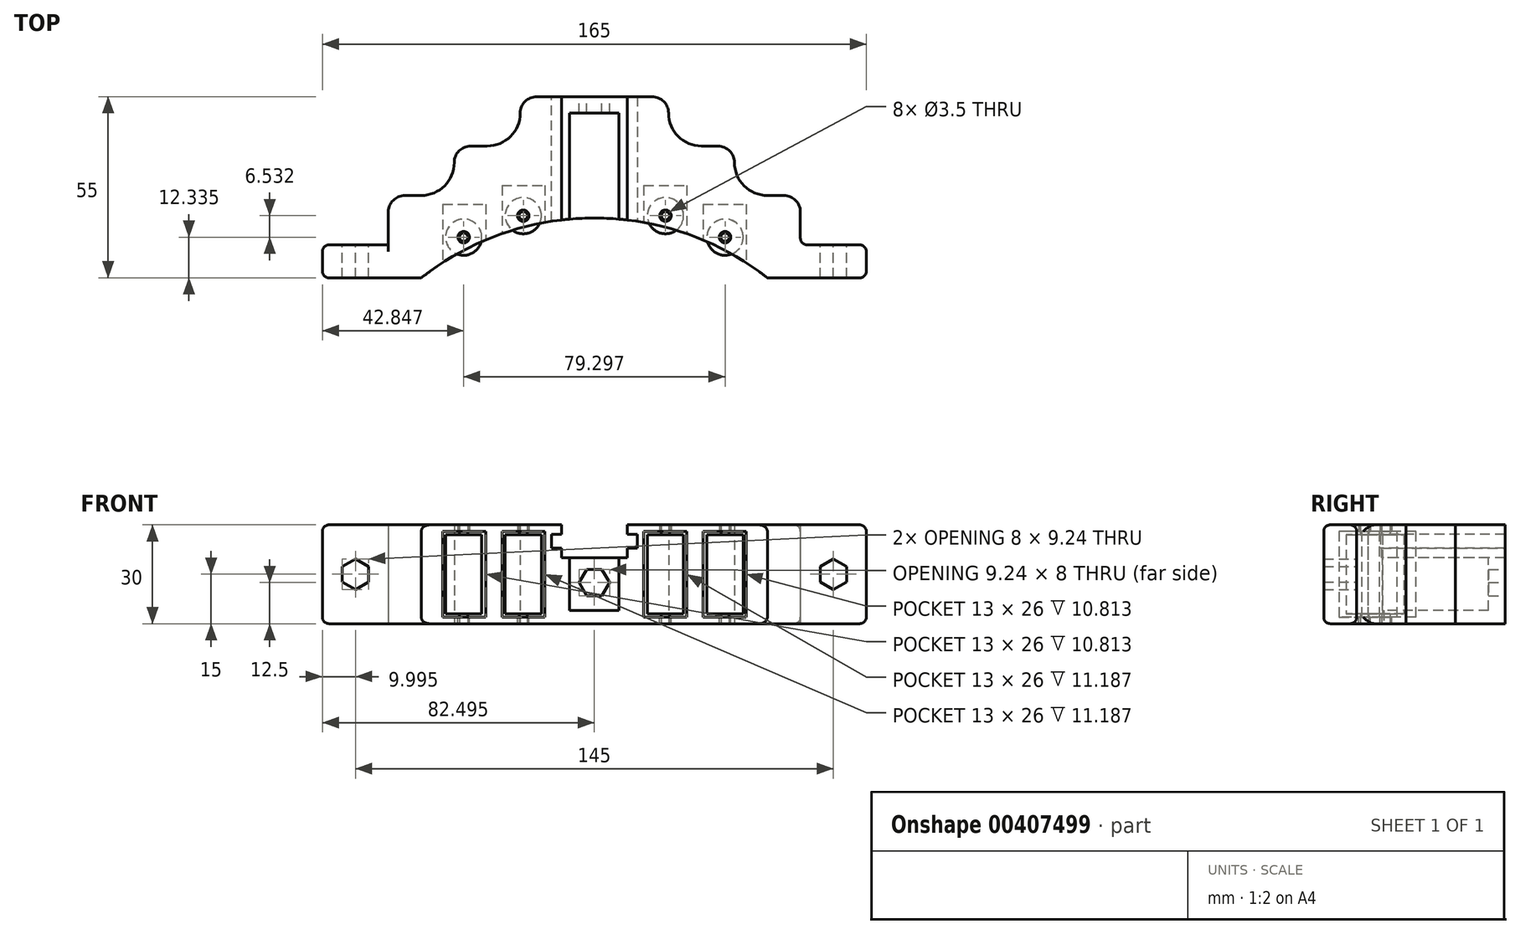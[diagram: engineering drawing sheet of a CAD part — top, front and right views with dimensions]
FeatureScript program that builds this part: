
annotation { "Feature Type Name" : "Feature", "Feature Type Description" : "" }
export const myFeature = defineFeature(function(context is Context, id is Id, definition is map)
    precondition{}
    {
        {
            var Q0;
            Q0=qCreatedBy(makeId("Top.planeOp"),FACE);
            var sketch = newSketch(context, id + "F0", { "sketchPlane" : qUnion([Q0])});
            skLineSegment(sketch, "E0", {"start": v(-87.77, -10.35) * mm, "end": v(-57.77, -10.35) * mm});
            skLineSegment(sketch, "E1", {"start": v(47.23, -10.35) * mm, "end": v(77.23, -10.35) * mm});
            skArc(sketch, "E2", {"start": v(47.23, -10.35) * mm, "mid": v(-5.27, 7.8) * mm, "end": v(-57.77, -10.35) * mm});
            skLineSegment(sketch, "E3", {"start": v(-87.77, -10.35) * mm, "end": v(-87.77, -0.35) * mm});
            skLineSegment(sketch, "E4", {"start": v(-87.77, -0.35) * mm, "end": v(-67.77, -0.35) * mm});
            skLineSegment(sketch, "E5", {"start": v(-67.77, -0.35) * mm, "end": v(-67.77, 14.65) * mm});
            skLineSegment(sketch, "E6", {"start": v(-67.77, 14.65) * mm, "end": v(-47.77, 14.65) * mm});
            skLineSegment(sketch, "E7", {"start": v(-47.77, 14.65) * mm, "end": v(-47.77, 29.65) * mm});
            skLineSegment(sketch, "E8", {"start": v(-47.77, 29.65) * mm, "end": v(-27.77, 29.65) * mm});
            skLineSegment(sketch, "E9", {"start": v(-27.77, 29.65) * mm, "end": v(-27.77, 44.65) * mm});
            skLineSegment(sketch, "E10", {"start": v(-5.27, -77.2) * mm, "end": v(-5.27, 79.15) * mm, "construction": true});
            skPoint(sketch, "E10.endSnap0", {"position": v(-5.27, 7.8) * mm});
            skLineSegment(sketch, "E11", {"start": v(77.23, -10.35) * mm, "end": v(77.23, -0.35) * mm});
            skLineSegment(sketch, "E12", {"start": v(77.23, -0.35) * mm, "end": v(57.23, -0.35) * mm});
            skLineSegment(sketch, "E13", {"start": v(57.23, -0.35) * mm, "end": v(57.23, 14.65) * mm});
            skLineSegment(sketch, "E14", {"start": v(57.23, 14.65) * mm, "end": v(37.23, 14.65) * mm});
            skLineSegment(sketch, "E15", {"start": v(37.23, 14.65) * mm, "end": v(37.23, 29.65) * mm});
            skLineSegment(sketch, "E16", {"start": v(37.23, 29.65) * mm, "end": v(17.23, 29.65) * mm});
            skLineSegment(sketch, "E17", {"start": v(17.23, 29.65) * mm, "end": v(17.23, 44.65) * mm});
            skLineSegment(sketch, "E18", {"start": v(-27.77, 44.65) * mm, "end": v(17.23, 44.65) * mm});
            skSolve(sketch);
        }
        {
            var Q0;
            Q0=makeQuery(id+"F0.imprint","IMPRINT",FACE,{"disambiguationData":[TD([[makeQuery(id+"F0.imprint","IMPRINT",EDGE,{"derivedFrom":sQuery(id+"F0.wireOp",EDGE,"E0")}),1.0]])]});
            extrude(context, id + "F1", {"entities" : qUnion([Q0]), "depth" : 30 * mm});
        }
        {
            var Q0;
            Q0=makeQuery(id+"F1.opExtrude","SWEPT_EDGE",EDGE,{"disambiguationData":[OSD([sQuery(id+"F0.wireOp",EDGE,"E6"),sQuery(id+"F0.wireOp",EDGE,"E7")])]});
            var Q1;
            Q1=makeQuery(id+"F1.opExtrude","SWEPT_EDGE",EDGE,{"disambiguationData":[OSD([sQuery(id+"F0.wireOp",EDGE,"E8"),sQuery(id+"F0.wireOp",EDGE,"E9")])]});
            var Q2;
            Q2=makeQuery(id+"F1.opExtrude","SWEPT_EDGE",EDGE,{"disambiguationData":[OSD([sQuery(id+"F0.wireOp",EDGE,"E16"),sQuery(id+"F0.wireOp",EDGE,"E17")])]});
            var Q3;
            Q3=makeQuery(id+"F1.opExtrude","SWEPT_EDGE",EDGE,{"disambiguationData":[OSD([sQuery(id+"F0.wireOp",EDGE,"E14"),sQuery(id+"F0.wireOp",EDGE,"E15")])]});
            fillet(context, id + "F2", {"entities" : qUnion([Q0, Q1, Q2, Q3]), "radius" : 10 * mm, "tangentPropagation" : true, "allowEdgeOverflow" : false});
        }
        {
            var Q0;
            Q0=makeQuery(id+"F1.opExtrude","SWEPT_EDGE",EDGE,{"disambiguationData":[OSD([sQuery(id+"F0.wireOp",EDGE,"E5"),sQuery(id+"F0.wireOp",EDGE,"E6")])]});
            var Q1;
            Q1=makeQuery(id+"F1.opExtrude","SWEPT_EDGE",EDGE,{"disambiguationData":[OSD([sQuery(id+"F0.wireOp",EDGE,"E7"),sQuery(id+"F0.wireOp",EDGE,"E8")])]});
            var Q2;
            Q2=makeQuery(id+"F1.opExtrude","SWEPT_EDGE",EDGE,{"disambiguationData":[OSD([sQuery(id+"F0.wireOp",EDGE,"E9"),sQuery(id+"F0.wireOp",EDGE,"E18")])]});
            var Q3;
            Q3=makeQuery(id+"F1.opExtrude","SWEPT_EDGE",EDGE,{"disambiguationData":[OSD([sQuery(id+"F0.wireOp",EDGE,"E17"),sQuery(id+"F0.wireOp",EDGE,"E18")])]});
            var Q4;
            Q4=makeQuery(id+"F1.opExtrude","SWEPT_EDGE",EDGE,{"disambiguationData":[OSD([sQuery(id+"F0.wireOp",EDGE,"E15"),sQuery(id+"F0.wireOp",EDGE,"E16")])]});
            var Q5;
            Q5=makeQuery(id+"F1.opExtrude","SWEPT_EDGE",EDGE,{"disambiguationData":[OSD([sQuery(id+"F0.wireOp",EDGE,"E13"),sQuery(id+"F0.wireOp",EDGE,"E14")])]});
            fillet(context, id + "F3", {"entities" : qUnion([Q0, Q1, Q2, Q3, Q4, Q5]), "radius" : 5 * mm, "tangentPropagation" : true, "allowEdgeOverflow" : false});
        }
        {
            var Q0;
            Q0=makeQuery(id+"F1.opExtrude","SWEPT_FACE",FACE,{"disambiguationData":[OSD([sQuery(id+"F0.wireOp",EDGE,"E0")])]});
            cPlane(context, id + "F4", {"entities" : qUnion([Q0]), "cplaneType" : CPlaneType.OFFSET, "offset" : 0 * mm, "width" : 150 * mm, "height" : 150 * mm});
        }
        {
            var Q0;
            Q0=qCreatedBy(id+"F4.planeOp",FACE);
            var sketch = newSketch(context, id + "F5", { "sketchPlane" : qUnion([Q0])});
            skLineSegment(sketch, "E19", {"start": v(-51.27, 28) * mm, "end": v(-38.27, 28) * mm});
            skLineSegment(sketch, "E20", {"start": v(-38.27, 28) * mm, "end": v(-38.27, 2) * mm});
            skLineSegment(sketch, "E21", {"start": v(-38.27, 2) * mm, "end": v(-51.27, 2) * mm});
            skLineSegment(sketch, "E22", {"start": v(-51.27, 2) * mm, "end": v(-51.27, 28) * mm});
            skLineSegment(sketch, "E23", {"start": v(-33.27, 28) * mm, "end": v(-20.27, 28) * mm});
            skLineSegment(sketch, "E24", {"start": v(-20.27, 28) * mm, "end": v(-20.27, 2) * mm});
            skLineSegment(sketch, "E25", {"start": v(-20.27, 2) * mm, "end": v(-33.27, 2) * mm});
            skLineSegment(sketch, "E26", {"start": v(-33.27, 2) * mm, "end": v(-33.27, 28) * mm});
            skLineSegment(sketch, "E27", {"start": v(9.73, 28) * mm, "end": v(22.73, 28) * mm});
            skLineSegment(sketch, "E28", {"start": v(22.73, 28) * mm, "end": v(22.73, 2) * mm});
            skLineSegment(sketch, "E29", {"start": v(22.73, 2) * mm, "end": v(9.73, 2) * mm});
            skLineSegment(sketch, "E30", {"start": v(9.73, 2) * mm, "end": v(9.73, 28) * mm});
            skLineSegment(sketch, "E31", {"start": v(27.73, 28) * mm, "end": v(40.73, 28) * mm});
            skLineSegment(sketch, "E32", {"start": v(40.73, 28) * mm, "end": v(40.73, 2) * mm});
            skLineSegment(sketch, "E33", {"start": v(40.73, 2) * mm, "end": v(27.73, 2) * mm});
            skLineSegment(sketch, "E34", {"start": v(27.73, 2) * mm, "end": v(27.73, 28) * mm});
            skSolve(sketch);
        }
        {
            var Q0;
            Q0=makeQuery(id+"F5.imprint","IMPRINT",FACE,{"disambiguationData":[TD([[makeQuery(id+"F5.imprint","IMPRINT",EDGE,{"derivedFrom":sQuery(id+"F5.wireOp",EDGE,"E19")}),-1.0]])]});
            var Q1;
            Q1=makeQuery(id+"F5.imprint","IMPRINT",FACE,{"disambiguationData":[TD([[makeQuery(id+"F5.imprint","IMPRINT",EDGE,{"derivedFrom":sQuery(id+"F5.wireOp",EDGE,"E31")}),-1.0]])]});
            extrude(context, id + "F6", {"entities" : qUnion([Q0, Q1]), "operationType" : NewBodyOperationType.REMOVE, "oppositeDirection" : true, "depth" : 22.3 * mm});
        }
        {
            var Q0;
            Q0=makeQuery(id+"F5.imprint","IMPRINT",FACE,{"disambiguationData":[TD([[makeQuery(id+"F5.imprint","IMPRINT",EDGE,{"derivedFrom":sQuery(id+"F5.wireOp",EDGE,"E23")}),-1.0]])]});
            var Q1;
            Q1=makeQuery(id+"F5.imprint","IMPRINT",FACE,{"disambiguationData":[TD([[makeQuery(id+"F5.imprint","IMPRINT",EDGE,{"derivedFrom":sQuery(id+"F5.wireOp",EDGE,"E27")}),-1.0]])]});
            extrude(context, id + "F7", {"entities" : qUnion([Q0, Q1]), "operationType" : NewBodyOperationType.REMOVE, "oppositeDirection" : true, "depth" : 28 * mm});
        }
        {
            var Q0;
            Q0=makeQuery(id+"F1.opExtrude","CAP_FACE",FACE,{"disambiguationData":[OSD([sQuery(id+"F0.wireOp",EDGE,"E0"),sQuery(id+"F0.wireOp",EDGE,"E1"),sQuery(id+"F0.wireOp",EDGE,"E2"),sQuery(id+"F0.wireOp",EDGE,"E3"),sQuery(id+"F0.wireOp",EDGE,"E4"),sQuery(id+"F0.wireOp",EDGE,"E5"),sQuery(id+"F0.wireOp",EDGE,"E6"),sQuery(id+"F0.wireOp",EDGE,"E7"),sQuery(id+"F0.wireOp",EDGE,"E8"),sQuery(id+"F0.wireOp",EDGE,"E9"),sQuery(id+"F0.wireOp",EDGE,"E11"),sQuery(id+"F0.wireOp",EDGE,"E12"),sQuery(id+"F0.wireOp",EDGE,"E13"),sQuery(id+"F0.wireOp",EDGE,"E14"),sQuery(id+"F0.wireOp",EDGE,"E15"),sQuery(id+"F0.wireOp",EDGE,"E16"),sQuery(id+"F0.wireOp",EDGE,"E17"),sQuery(id+"F0.wireOp",EDGE,"E18")])],"isStart":false});
            var sketch = newSketch(context, id + "F8", { "sketchPlane" : qUnion([Q0])});
            skLineSegment(sketch, "E35.bottom", {"start": v(-15.27, 44.65) * mm, "end": v(4.73, 44.65) * mm});
            skLineSegment(sketch, "E35.top", {"start": v(-15.27, 7.2) * mm, "end": v(4.73, 7.2) * mm});
            skLineSegment(sketch, "E35.left", {"start": v(-15.27, 44.65) * mm, "end": v(-15.27, 7.2) * mm});
            skLineSegment(sketch, "E35.right", {"start": v(4.73, 44.65) * mm, "end": v(4.73, 7.2) * mm});
            skSolve(sketch);
        }
        {
            var Q0;
            Q0=makeQuery(id+"F8.imprint","IMPRINT",FACE,{"disambiguationData":[TD([[makeQuery(id+"F8.imprint","IMPRINT",EDGE,{"derivedFrom":sQuery(id+"F8.wireOp",EDGE,"E35.bottom")}),-1.0]])]});
            extrude(context, id + "F9", {"entities" : qUnion([Q0]), "operationType" : NewBodyOperationType.REMOVE, "oppositeDirection" : true, "depth" : 10 * mm});
        }
        {
            var Q0;
            Q0=makeQuery(id+"F9.boolean.opBoolean","COPY",FACE,{"derivedFrom":makeQuery(id+"F9.opExtrude","CAP_FACE",FACE,{"disambiguationData":[OSD([sQuery(id+"F0.wireOp",EDGE,"E2"),sQuery(id+"F8.wireOp",EDGE,"E35.bottom"),sQuery(id+"F8.wireOp",EDGE,"E35.left"),sQuery(id+"F8.wireOp",EDGE,"E35.right")])],"isStart":false})});
            var sketch = newSketch(context, id + "F10", { "sketchPlane" : qUnion([Q0])});
            skLineSegment(sketch, "E36.bottom", {"start": v(-12.77, 39.65) * mm, "end": v(2.23, 39.65) * mm});
            skLineSegment(sketch, "E36.top", {"start": v(-12.77, 1.65) * mm, "end": v(2.23, 1.65) * mm});
            skLineSegment(sketch, "E36.left", {"start": v(-12.77, 39.65) * mm, "end": v(-12.77, 1.65) * mm});
            skLineSegment(sketch, "E36.right", {"start": v(2.23, 39.65) * mm, "end": v(2.23, 1.65) * mm});
            skSolve(sketch);
        }
        {
            var Q0;
            Q0=makeQuery(id+"F10.imprint","IMPRINT",FACE,{"disambiguationData":[TD([[makeQuery(id+"F10.imprint","IMPRINT",EDGE,{"derivedFrom":sQuery(id+"F10.wireOp",EDGE,"E36.bottom")}),-1.0]])]});
            extrude(context, id + "F11", {"entities" : qUnion([Q0]), "operationType" : NewBodyOperationType.REMOVE, "oppositeDirection" : true, "depth" : 16 * mm});
        }
        {
            var Q0;
            Q0=makeQuery(id+"F9.boolean.opBoolean","COPY",FACE,{"derivedFrom":makeQuery(id+"F9.opExtrude","SWEPT_FACE",FACE,{"disambiguationData":[OSD([sQuery(id+"F8.wireOp",EDGE,"E35.right")])]})});
            var sketch = newSketch(context, id + "F12", { "sketchPlane" : qUnion([Q0])});
            skLineSegment(sketch, "E37.bottom", {"start": v(-44.65, 27.1) * mm, "end": v(-6.65, 27.1) * mm});
            skLineSegment(sketch, "E37.top", {"start": v(-44.65, 22.9) * mm, "end": v(-6.65, 22.9) * mm});
            skLineSegment(sketch, "E37.left", {"start": v(-44.65, 27.1) * mm, "end": v(-44.65, 22.9) * mm});
            skLineSegment(sketch, "E37.right", {"start": v(-6.65, 27.1) * mm, "end": v(-6.65, 22.9) * mm});
            skSolve(sketch);
        }
        {
            var Q0;
            Q0=makeQuery(id+"F9.boolean.opBoolean","COPY",FACE,{"derivedFrom":makeQuery(id+"F9.opExtrude","SWEPT_FACE",FACE,{"disambiguationData":[OSD([sQuery(id+"F8.wireOp",EDGE,"E35.left")])]})});
            var sketch = newSketch(context, id + "F13", { "sketchPlane" : qUnion([Q0])});
            skLineSegment(sketch, "E38.bottom", {"start": v(6.65, 27.1) * mm, "end": v(44.65, 27.1) * mm});
            skLineSegment(sketch, "E38.top", {"start": v(6.65, 22.9) * mm, "end": v(44.65, 22.9) * mm});
            skLineSegment(sketch, "E38.left", {"start": v(6.65, 27.1) * mm, "end": v(6.65, 22.9) * mm});
            skLineSegment(sketch, "E38.right", {"start": v(44.65, 27.1) * mm, "end": v(44.65, 22.9) * mm});
            skSolve(sketch);
        }
        {
            var Q0;
            Q0=makeQuery(id+"F12.imprint","IMPRINT",FACE,{"disambiguationData":[TD([[makeQuery(id+"F12.imprint","IMPRINT",EDGE,{"derivedFrom":sQuery(id+"F12.wireOp",EDGE,"E37.bottom")}),-1.0]])]});
            var Q1;
            Q1=makeQuery(id+"F13.imprint","IMPRINT",FACE,{"disambiguationData":[TD([[makeQuery(id+"F13.imprint","IMPRINT",EDGE,{"derivedFrom":sQuery(id+"F13.wireOp",EDGE,"E38.bottom")}),-1.0]])]});
            extrude(context, id + "F14", {"entities" : qUnion([Q0, Q1]), "operationType" : NewBodyOperationType.REMOVE, "oppositeDirection" : true, "depth" : 3 * mm, "hasSecondDirection" : true, "secondDirectionOppositeDirection" : false, "secondDirectionDepth" : 3 * mm});
        }
        {
            var Q0;
            Q0=makeQuery(id+"F1.opExtrude","SWEPT_FACE",FACE,{"disambiguationData":[OSD([sQuery(id+"F0.wireOp",EDGE,"E18")])]});
            var sketch = newSketch(context, id + "F15", { "sketchPlane" : qUnion([Q0])});
            skCircle(sketch, "E39.cCircle", {"center": v(5.27, 12.5) * mm, "radius": 4 * mm, "construction": true});
            skLineSegment(sketch, "E39.0", {"start": v(9.9, 12.5) * mm, "end": v(7.58, 8.5) * mm});
            skLineSegment(sketch, "E39.1", {"start": v(7.58, 8.5) * mm, "end": v(2.97, 8.5) * mm});
            skLineSegment(sketch, "E39.2", {"start": v(2.97, 8.5) * mm, "end": v(0.66, 12.5) * mm});
            skLineSegment(sketch, "E39.3", {"start": v(0.66, 12.5) * mm, "end": v(2.97, 16.5) * mm});
            skLineSegment(sketch, "E39.4", {"start": v(2.97, 16.5) * mm, "end": v(7.58, 16.5) * mm});
            skLineSegment(sketch, "E39.5", {"start": v(7.58, 16.5) * mm, "end": v(9.9, 12.5) * mm});
            skPoint(sketch, "E39.0.midPoint", {"position": v(8.74, 10.5) * mm});
            skSolve(sketch);
        }
        {
            var Q0;
            Q0 = qSketchRegion(id + "F15", true);
            var Q1;
            Q1=makeQuery(id+"F11.boolean.opBoolean","COPY",FACE,{"derivedFrom":makeQuery(id+"F11.opExtrude","SWEPT_FACE",FACE,{"disambiguationData":[OSD([sQuery(id+"F10.wireOp",EDGE,"E36.bottom")])]})});
            extrude(context, id + "F16", {"entities" : qUnion([Q0]), "operationType" : NewBodyOperationType.REMOVE, "endBound" : BoundingType.UP_TO_SURFACE, "oppositeDirection" : true, "endBoundEntityFace" : qUnion([Q1]), "depth" : 25 * mm});
        }
        {
            var Q0;
            Q0=makeQuery(id+"F6.boolean.opBoolean","COPY",FACE,{"derivedFrom":makeQuery(id+"F6.opExtrude","SWEPT_FACE",FACE,{"disambiguationData":[OSD([sQuery(id+"F5.wireOp",EDGE,"E21")])]})});
            var sketch = newSketch(context, id + "F17", { "sketchPlane" : qUnion([Q0])});
            skCircle(sketch, "E40", {"center": v(-44.92, 1.98) * mm, "radius": 1.75 * mm});
            skCircle(sketch, "E41", {"center": v(-26.84, 8.52) * mm, "radius": 1.75 * mm});
            skCircle(sketch, "E42", {"center": v(16.3, 8.52) * mm, "radius": 1.75 * mm});
            skCircle(sketch, "E43", {"center": v(34.37, 1.98) * mm, "radius": 1.75 * mm});
            skSolve(sketch);
        }
        {
            var Q0;
            Q0 = qSketchRegion(id + "F17", true);
            extrude(context, id + "F18", {"entities" : qUnion([Q0]), "operationType" : NewBodyOperationType.REMOVE, "endBound" : BoundingType.THROUGH_ALL, "oppositeDirection" : true, "depth" : 25 * mm});
        }
        {
            var Q0;
            Q0=makeQuery(id+"F1.opExtrude","CAP_FACE",FACE,{"disambiguationData":[OSD([sQuery(id+"F0.wireOp",EDGE,"E0"),sQuery(id+"F0.wireOp",EDGE,"E1"),sQuery(id+"F0.wireOp",EDGE,"E2"),sQuery(id+"F0.wireOp",EDGE,"E3"),sQuery(id+"F0.wireOp",EDGE,"E4"),sQuery(id+"F0.wireOp",EDGE,"E5"),sQuery(id+"F0.wireOp",EDGE,"E6"),sQuery(id+"F0.wireOp",EDGE,"E7"),sQuery(id+"F0.wireOp",EDGE,"E8"),sQuery(id+"F0.wireOp",EDGE,"E9"),sQuery(id+"F0.wireOp",EDGE,"E11"),sQuery(id+"F0.wireOp",EDGE,"E12"),sQuery(id+"F0.wireOp",EDGE,"E13"),sQuery(id+"F0.wireOp",EDGE,"E14"),sQuery(id+"F0.wireOp",EDGE,"E15"),sQuery(id+"F0.wireOp",EDGE,"E16"),sQuery(id+"F0.wireOp",EDGE,"E17"),sQuery(id+"F0.wireOp",EDGE,"E18")])],"isStart":true});
            var sketch = newSketch(context, id + "F19", { "sketchPlane" : qUnion([Q0])});
            skCircle(sketch, "E44", {"center": v(-44.92, -1.98) * mm, "radius": 1.25 * mm});
            skCircle(sketch, "E45", {"center": v(-26.84, -8.52) * mm, "radius": 1.25 * mm});
            skCircle(sketch, "E46", {"center": v(16.3, -8.52) * mm, "radius": 1.25 * mm});
            skCircle(sketch, "E47", {"center": v(34.37, -1.98) * mm, "radius": 1.25 * mm});
            skSolve(sketch);
        }
        {
            var Q0;
            Q0 = qSketchRegion(id + "F19", true);
            extrude(context, id + "F20", {"entities" : qUnion([Q0]), "oppositeDirection" : true, "depth" : 3 * mm});
        }
        {
            var Q0;
            Q0=makeQuery(id+"F20.opExtrude","CAP_FACE",FACE,{"disambiguationData":[OSD([sQuery(id+"F19.wireOp",EDGE,"E44")])],"isStart":false});
            var sketch = newSketch(context, id + "F21", { "sketchPlane" : qUnion([Q0])});
            skCircle(sketch, "E48", {"center": v(-44.92, 1.98) * mm, "radius": 5.5 * mm});
            skCircle(sketch, "E49", {"center": v(-26.84, 8.52) * mm, "radius": 5.5 * mm});
            skCircle(sketch, "E50", {"center": v(16.3, 8.52) * mm, "radius": 5.5 * mm});
            skCircle(sketch, "E51", {"center": v(34.37, 1.98) * mm, "radius": 5.5 * mm});
            skSolve(sketch);
        }
        {
            var Q0;
            Q0 = qSketchRegion(id + "F21", true);
            extrude(context, id + "F22", {"entities" : qUnion([Q0]), "depth" : 24 * mm});
        }
        {
            var Q0;
            Q0=makeQuery(id+"F6.boolean.opBoolean","COPY",FACE,{"derivedFrom":makeQuery(id+"F6.opExtrude","SWEPT_FACE",FACE,{"disambiguationData":[OSD([sQuery(id+"F5.wireOp",EDGE,"E19")])]})});
            var sketch = newSketch(context, id + "F23", { "sketchPlane" : qUnion([Q0])});
            skCircle(sketch, "E52", {"center": v(-44.92, -1.98) * mm, "radius": 1.75 * mm});
            skCircle(sketch, "E53", {"center": v(-26.84, -8.52) * mm, "radius": 1.75 * mm});
            skCircle(sketch, "E54", {"center": v(16.3, -8.52) * mm, "radius": 1.75 * mm});
            skCircle(sketch, "E55", {"center": v(34.37, -1.98) * mm, "radius": 1.75 * mm});
            skSolve(sketch);
        }
        {
            var Q0;
            Q0 = qSketchRegion(id + "F23", true);
            extrude(context, id + "F24", {"entities" : qUnion([Q0]), "operationType" : NewBodyOperationType.REMOVE, "endBound" : BoundingType.THROUGH_ALL, "oppositeDirection" : true, "depth" : 25 * mm});
        }
        {
            var Q0;
            Q0=makeQuery(id+"F22.opExtrude","CAP_FACE",FACE,{"disambiguationData":[OSD([sQuery(id+"F21.wireOp",EDGE,"E48")])],"isStart":false});
            var sketch = newSketch(context, id + "F25", { "sketchPlane" : qUnion([Q0])});
            skCircle(sketch, "E56", {"center": v(-44.92, 1.98) * mm, "radius": 1.25 * mm});
            skCircle(sketch, "E57", {"center": v(-26.84, 8.52) * mm, "radius": 1.25 * mm});
            skCircle(sketch, "E58", {"center": v(16.3, 8.52) * mm, "radius": 1.25 * mm});
            skCircle(sketch, "E59", {"center": v(34.37, 1.98) * mm, "radius": 1.25 * mm});
            skSolve(sketch);
        }
        {
            var Q0;
            Q0 = qSketchRegion(id + "F25", true);
            var Q1;
            {var subQ0=sQuery(id+"F0.wireOp",EDGE,"E8");var subQ1=sQuery(id+"F0.wireOp",EDGE,"E7");var subQ2=sQuery(id+"F0.wireOp",EDGE,"E18");var subQ3=sQuery(id+"F0.wireOp",EDGE,"E6");var subQ4=sQuery(id+"F0.wireOp",EDGE,"E5");var subQ5=sQuery(id+"F0.wireOp",EDGE,"E9");var subQ6=sQuery(id+"F0.wireOp",EDGE,"E0");var subQ7=sQuery(id+"F0.wireOp",EDGE,"E3");var subQ8=sQuery(id+"F0.wireOp",EDGE,"E2");var subQ9=sQuery(id+"F0.wireOp",EDGE,"E4");Q1=makeQuery(id+"F9.boolean.opBoolean","SPLIT",FACE,{"disambiguationData":[TD([makeQuery(id+"F1.opExtrude","SWEPT_FACE",FACE,{"disambiguationData":[OSD([subQ6])]})])],"derivedFrom":makeQuery(id+"F1.opExtrude","CAP_FACE",FACE,{"disambiguationData":[OSD([subQ6,sQuery(id+"F0.wireOp",EDGE,"E1"),subQ8,subQ7,subQ9,subQ4,subQ3,subQ1,subQ0,subQ5,sQuery(id+"F0.wireOp",EDGE,"E11"),sQuery(id+"F0.wireOp",EDGE,"E12"),sQuery(id+"F0.wireOp",EDGE,"E13"),sQuery(id+"F0.wireOp",EDGE,"E14"),sQuery(id+"F0.wireOp",EDGE,"E15"),sQuery(id+"F0.wireOp",EDGE,"E16"),sQuery(id+"F0.wireOp",EDGE,"E17"),subQ2])],"isStart":false})});}
            extrude(context, id + "F26", {"entities" : qUnion([Q0]), "operationType" : NewBodyOperationType.ADD, "endBound" : BoundingType.UP_TO_SURFACE, "endBoundEntityFace" : qUnion([Q1]), "depth" : 25 * mm});
        }
        {
            var Q0;
            Q0=makeQuery(id+"F1.opExtrude","SWEPT_FACE",FACE,{"disambiguationData":[OSD([sQuery(id+"F0.wireOp",EDGE,"E4")])]});
            var sketch = newSketch(context, id + "F27", { "sketchPlane" : qUnion([Q0])});
            skCircle(sketch, "E60.cCircle", {"center": v(77.77, 15) * mm, "radius": 4 * mm, "construction": true});
            skPoint(sketch, "E60.cCircle.centerSnap0", {"position": v(87.77, 15) * mm});
            skLineSegment(sketch, "E60.0", {"start": v(81.77, 12.7) * mm, "end": v(77.77, 10.38) * mm});
            skLineSegment(sketch, "E60.1", {"start": v(77.77, 10.38) * mm, "end": v(73.77, 12.7) * mm});
            skLineSegment(sketch, "E60.2", {"start": v(73.77, 12.7) * mm, "end": v(73.77, 17.3) * mm});
            skLineSegment(sketch, "E60.3", {"start": v(73.77, 17.3) * mm, "end": v(77.77, 19.62) * mm});
            skLineSegment(sketch, "E60.4", {"start": v(77.77, 19.62) * mm, "end": v(81.77, 17.3) * mm});
            skLineSegment(sketch, "E60.5", {"start": v(81.77, 17.3) * mm, "end": v(81.77, 12.7) * mm});
            skPoint(sketch, "E60.0.midPoint", {"position": v(79.77, 11.54) * mm});
            skSolve(sketch);
        }
        {
            var Q0;
            Q0=makeQuery(id+"F1.opExtrude","SWEPT_FACE",FACE,{"disambiguationData":[OSD([sQuery(id+"F0.wireOp",EDGE,"E12")])]});
            var sketch = newSketch(context, id + "F28", { "sketchPlane" : qUnion([Q0])});
            skCircle(sketch, "E61.cCircle", {"center": v(-67.23, 15) * mm, "radius": 4 * mm, "construction": true});
            skLineSegment(sketch, "E61.0", {"start": v(-71.23, 12.7) * mm, "end": v(-71.23, 17.3) * mm});
            skLineSegment(sketch, "E61.1", {"start": v(-71.23, 17.3) * mm, "end": v(-67.23, 19.62) * mm});
            skLineSegment(sketch, "E61.2", {"start": v(-67.23, 19.62) * mm, "end": v(-63.23, 17.3) * mm});
            skLineSegment(sketch, "E61.3", {"start": v(-63.23, 17.3) * mm, "end": v(-63.23, 12.7) * mm});
            skLineSegment(sketch, "E61.4", {"start": v(-63.23, 12.7) * mm, "end": v(-67.23, 10.38) * mm});
            skLineSegment(sketch, "E61.5", {"start": v(-67.23, 10.38) * mm, "end": v(-71.23, 12.7) * mm});
            skPoint(sketch, "E61.0.midPoint", {"position": v(-71.23, 15) * mm});
            skSolve(sketch);
        }
        {
            var Q0;
            Q0 = qSketchRegion(id + "F28", true);
            var Q1;
            Q1 = qSketchRegion(id + "F27", true);
            extrude(context, id + "F29", {"entities" : qUnion([Q0, Q1]), "operationType" : NewBodyOperationType.REMOVE, "endBound" : BoundingType.THROUGH_ALL, "oppositeDirection" : true, "depth" : 25 * mm});
        }
        {
            var Q0;
            Q0=makeQuery(id+"F1.opExtrude","SWEPT_EDGE",EDGE,{"disambiguationData":[OSD([sQuery(id+"F0.wireOp",EDGE,"E3"),sQuery(id+"F0.wireOp",EDGE,"E4")])]});
            var Q1;
            Q1=makeQuery(id+"F1.opExtrude","SWEPT_EDGE",EDGE,{"disambiguationData":[OSD([sQuery(id+"F0.wireOp",EDGE,"E0"),sQuery(id+"F0.wireOp",EDGE,"E3")])]});
            var Q2;
            Q2=makeQuery(id+"F1.opExtrude","CAP_EDGE",EDGE,{"disambiguationData":[OSD([sQuery(id+"F0.wireOp",EDGE,"E3")])],"isStart":true});
            var Q3;
            Q3=makeQuery(id+"F1.opExtrude","CAP_EDGE",EDGE,{"disambiguationData":[OSD([sQuery(id+"F0.wireOp",EDGE,"E4")])],"isStart":true});
            var Q4;
            Q4=makeQuery(id+"F1.opExtrude","CAP_EDGE",EDGE,{"disambiguationData":[OSD([sQuery(id+"F0.wireOp",EDGE,"E4")])],"isStart":false});
            var Q5;
            Q5=makeQuery(id+"F1.opExtrude","CAP_EDGE",EDGE,{"disambiguationData":[OSD([sQuery(id+"F0.wireOp",EDGE,"E0")])],"isStart":false});
            var Q6;
            Q6=makeQuery(id+"F1.opExtrude","CAP_EDGE",EDGE,{"disambiguationData":[OSD([sQuery(id+"F0.wireOp",EDGE,"E0")])],"isStart":true});
            var Q7;
            Q7=makeQuery(id+"F1.opExtrude","CAP_EDGE",EDGE,{"disambiguationData":[OSD([sQuery(id+"F0.wireOp",EDGE,"E1")])],"isStart":true});
            var Q8;
            Q8=makeQuery(id+"F1.opExtrude","CAP_EDGE",EDGE,{"disambiguationData":[OSD([sQuery(id+"F0.wireOp",EDGE,"E12")])],"isStart":true});
            var Q9;
            Q9=makeQuery(id+"F1.opExtrude","CAP_EDGE",EDGE,{"disambiguationData":[OSD([sQuery(id+"F0.wireOp",EDGE,"E11")])],"isStart":true});
            var Q10;
            Q10=makeQuery(id+"F1.opExtrude","SWEPT_EDGE",EDGE,{"disambiguationData":[OSD([sQuery(id+"F0.wireOp",EDGE,"E11"),sQuery(id+"F0.wireOp",EDGE,"E12")])]});
            var Q11;
            Q11=makeQuery(id+"F1.opExtrude","SWEPT_EDGE",EDGE,{"disambiguationData":[OSD([sQuery(id+"F0.wireOp",EDGE,"E12"),sQuery(id+"F0.wireOp",EDGE,"E13")])]});
            var Q12;
            Q12=makeQuery(id+"F1.opExtrude","CAP_EDGE",EDGE,{"disambiguationData":[OSD([sQuery(id+"F0.wireOp",EDGE,"E12")])],"isStart":false});
            var Q13;
            Q13=makeQuery(id+"F1.opExtrude","CAP_EDGE",EDGE,{"disambiguationData":[OSD([sQuery(id+"F0.wireOp",EDGE,"E11")])],"isStart":false});
            var Q14;
            Q14=makeQuery(id+"F1.opExtrude","CAP_EDGE",EDGE,{"disambiguationData":[OSD([sQuery(id+"F0.wireOp",EDGE,"E1")])],"isStart":false});
            var Q15;
            Q15=makeQuery(id+"F1.opExtrude","SWEPT_EDGE",EDGE,{"disambiguationData":[OSD([sQuery(id+"F0.wireOp",EDGE,"E1"),sQuery(id+"F0.wireOp",EDGE,"E11")])]});
            var Q16;
            Q16=makeQuery(id+"F1.opExtrude","CAP_EDGE",EDGE,{"disambiguationData":[OSD([sQuery(id+"F0.wireOp",EDGE,"E3")])],"isStart":false});
            fillet(context, id + "F30", {"entities" : qUnion([Q0, Q1, Q2, Q3, Q4, Q5, Q6, Q7, Q8, Q9, Q10, Q11, Q12, Q13, Q14, Q15, Q16]), "radius" : 2 * mm, "tangentPropagation" : true, "allowEdgeOverflow" : false});
        }
    });
